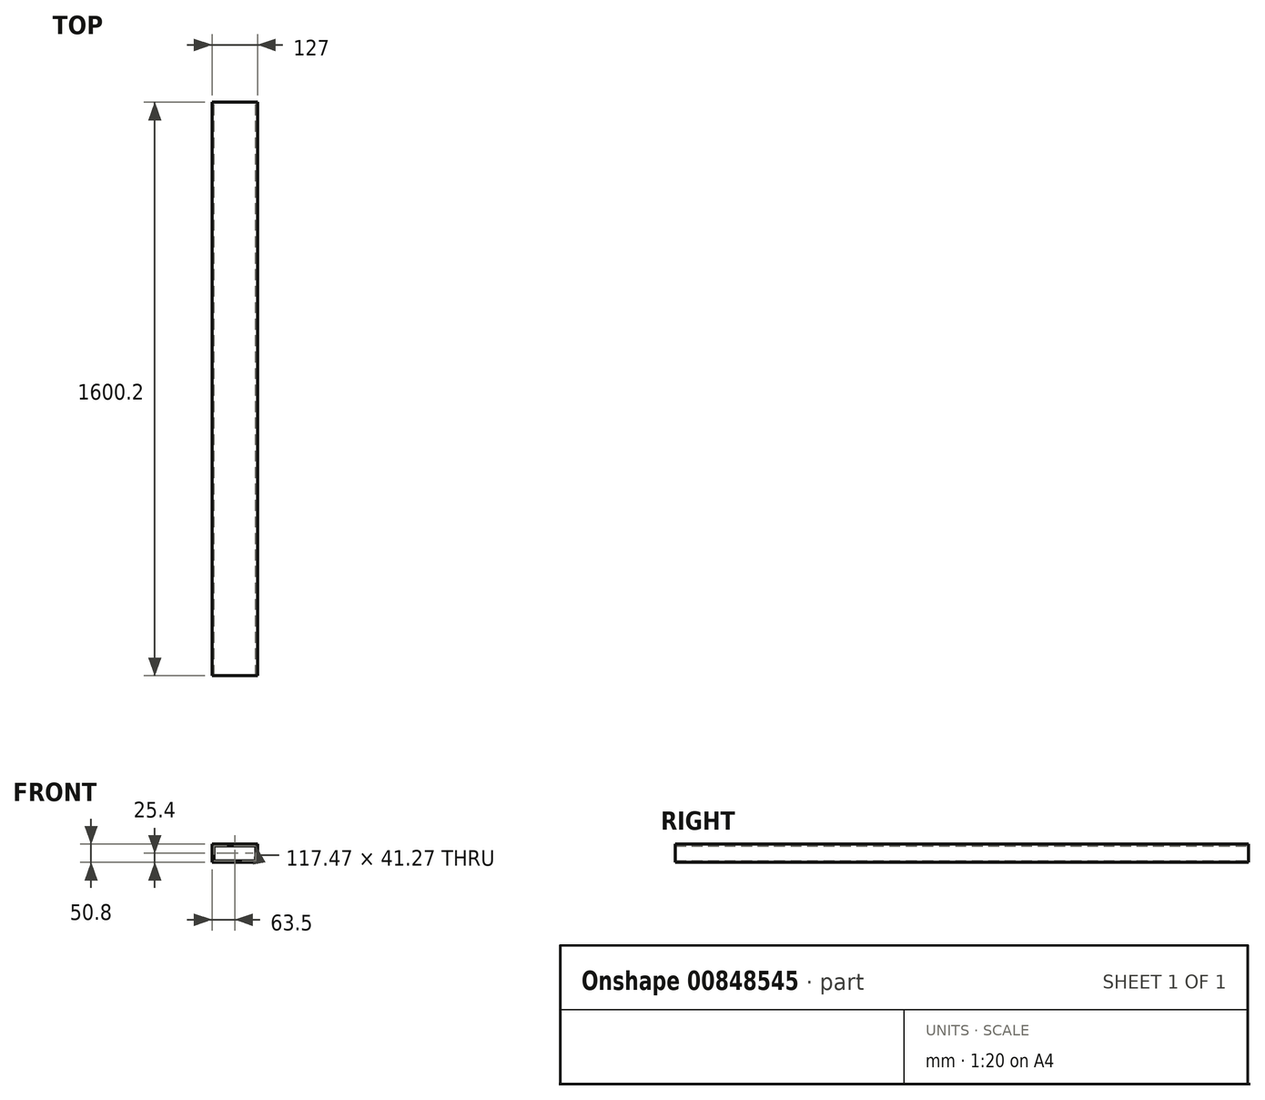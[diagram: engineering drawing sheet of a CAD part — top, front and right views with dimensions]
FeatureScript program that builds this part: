
annotation { "Feature Type Name" : "Feature", "Feature Type Description" : "" }
export const myFeature = defineFeature(function(context is Context, id is Id, definition is map)
    precondition{}
    {
        {
            var Q0;
            Q0=qCreatedBy(makeId("Top.planeOp"),FACE);
            var sketch = newSketch(context, id + "F0", { "sketchPlane" : qUnion([Q0])});
            skLineSegment(sketch, "E0.bottom", {"start": v(63.5, -800.1) * mm, "end": v(-63.5, -800.1) * mm});
            skLineSegment(sketch, "E0.top", {"start": v(63.5, 800.1) * mm, "end": v(-63.5, 800.1) * mm});
            skLineSegment(sketch, "E0.left", {"start": v(63.5, -800.1) * mm, "end": v(63.5, 800.1) * mm});
            skLineSegment(sketch, "E0.right", {"start": v(-63.5, -800.1) * mm, "end": v(-63.5, 800.1) * mm});
            skPoint(sketch, "E0.middle", {"position": v(0, 0) * mm});
            skSolve(sketch);
        }
        {
            var Q0;
            Q0=makeQuery(id+"F0.imprint","IMPRINT",FACE,{"disambiguationData":[TD([[makeQuery(id+"F0.imprint","IMPRINT",EDGE,{"derivedFrom":sQuery(id+"F0.wireOp",EDGE,"E0.bottom")}),-1.0]])]});
            extrude(context, id + "F1", {"entities" : qUnion([Q0]), "depth" : 50.8 * mm, "offsetDistance" : 25.4 * mm});
        }
        {
            var Q0;
            Q0=makeQuery(id+"F1.opExtrude","SWEPT_FACE",FACE,{"disambiguationData":[OSD([sQuery(id+"F0.wireOp",EDGE,"E0.bottom")])]});
            var Q1;
            Q1=makeQuery(id+"F1.opExtrude","SWEPT_FACE",FACE,{"disambiguationData":[OSD([sQuery(id+"F0.wireOp",EDGE,"E0.top")])]});
            shell(context, id + "F2", {"entities" : qUnion([Q0, Q1]), "thickness" : 4.76 * mm});
        }
    });
